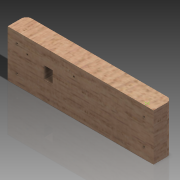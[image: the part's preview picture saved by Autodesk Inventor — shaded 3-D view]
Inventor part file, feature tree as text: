
AUTODESK INVENTOR PART (.ipt)
format: ipt  version: 2014 SP1 (Build 180222100, 222)  size: 155,648 bytes
history: native  units: mm
features: sketch x4, extrude x2, hole x1, fillet x1
ambient origin geometry x8: Origin, YZ Plane, XZ Plane, XY Plane, X Axis, Y Axis, Z Axis, Center Point
bodies: Volumenkörper1 (feature_tree)
feature tree (8):
  extrude  "Extrusion1"  Depth=45.0mm
  hole  "Bohrung1"  [1 undecoded]
  fillet  "Rundung3"  Radius=25.0mm
  extrude  "Extrusion2"  Depth=10.0mm
  sketch  "Skizze1"  dims[d0=140.0mm d1=45.0mm]
  sketch  "Skizze2"  dims[d2=18.0mm d3=0.0mm d14=10.0mm d15=25.0mm]
  sketch  "Skizze3"  dims[d16=10.0mm d17=25.0mm]
  sketch  "Skizze4"  dims[d18=9.0mm d19=9.0mm d20=2.0mm d21=6.0mm d22=5.0mm d23=2.0mm d24=90.0deg d25=8.0mm d26=20.594885mm d27=5.0mm d32=8.0mm d33=12.0mm d34=15.0mm d36=35.0mm d37=18.0mm d38=0.0mm]
note: 1 required parameter value undecoded (feature->parameter linkage not recoverable at this tier; creation-order binding heuristic only, values carry confidence <= 0.55)
